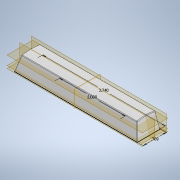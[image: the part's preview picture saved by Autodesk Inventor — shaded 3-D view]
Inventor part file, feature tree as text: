
AUTODESK INVENTOR PART (.ipt)
format: ipt  version: 2022 (Build 260153000, 153)  size: 292,352 bytes
history: native  units: in
note: dims shown in document units (in); Inventor stores cm internally (conversion verified against a paired STEP export)
features: sketch x7, extrude x6, other x4, mirror x1, shell x1, fillet x1
ambient origin geometry x8: Origin, YZ Plane, XZ Plane, XY Plane, X Axis, Y Axis, Z Axis, Center Point
bodies: Body1 (feature_tree)
feature tree (20):
  other  "ソリッド1"
  sketch  "スケッチ1"
  extrude  "押し出し1"  Depth=0.7087in
  extrude  "押し出し2"  Depth=3.7402in
  other  "作業平面1"
  extrude  "押し出し3"  Depth=2.0in
  mirror  "ミラー1"
  sketch  "スケッチ7"
  shell  "シェル1"  Thickness=0.463in
  extrude  "押し出し4"  Depth=0.5841in
  other  "作業平面2"
  extrude  "押し出し5"  Depth=0.5209in
  fillet  "フィレット2"  Radius=0.4331in
  other  "作業平面3"
  extrude  "押し出し6"  TaperAngle=0.0deg  [1 undecoded]
  sketch  "スケッチ2"
  sketch  "スケッチ3"
  sketch  "スケッチ5"
  sketch  "スケッチ8"
  sketch  "スケッチ9"
note: 1 required parameter value undecoded (feature->parameter linkage not recoverable at this tier; creation-order binding heuristic only, values carry confidence <= 0.55)
